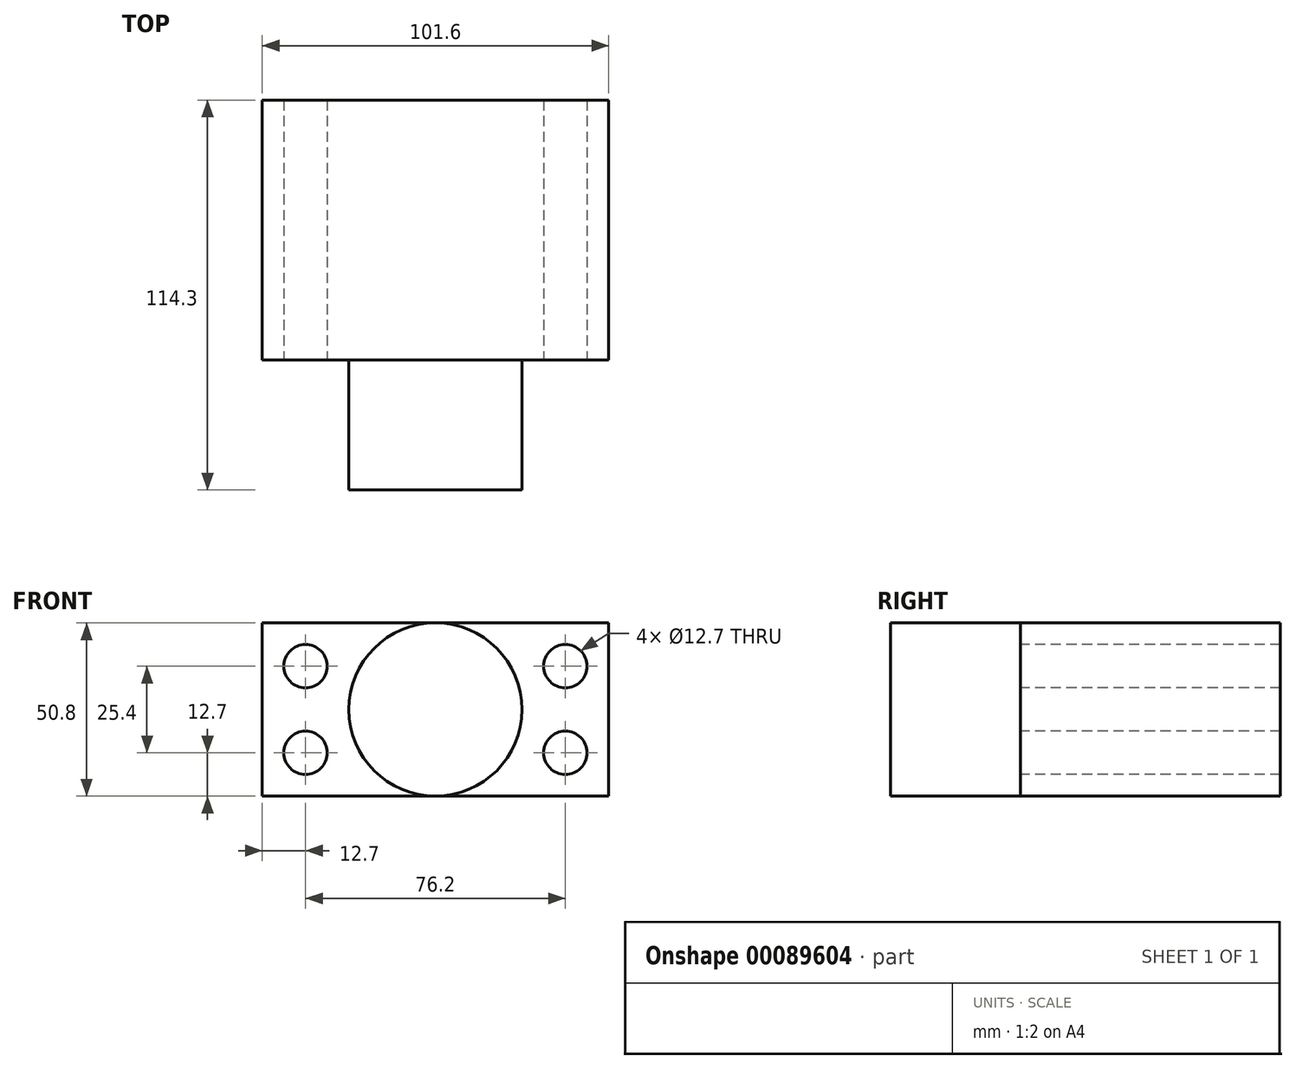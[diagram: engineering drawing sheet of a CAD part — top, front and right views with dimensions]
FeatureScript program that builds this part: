
annotation { "Feature Type Name" : "Feature", "Feature Type Description" : "" }
export const myFeature = defineFeature(function(context is Context, id is Id, definition is map)
    precondition{}
    {
        {
            var Q0;
            Q0=qCreatedBy(makeId("Front.planeOp"),FACE);
            var sketch = newSketch(context, id + "F0", { "sketchPlane" : qUnion([Q0])});
            skLineSegment(sketch, "E0", {"start": v(-50.8, 25.4) * mm, "end": v(50.8, 25.4) * mm});
            skLineSegment(sketch, "E1", {"start": v(50.8, 25.4) * mm, "end": v(50.8, -25.4) * mm});
            skLineSegment(sketch, "E2", {"start": v(50.8, -25.4) * mm, "end": v(-50.8, -25.4) * mm});
            skLineSegment(sketch, "E3", {"start": v(-50.8, 25.4) * mm, "end": v(-50.8, -25.4) * mm});
            skSolve(sketch);
        }
        {
            var Q0;
            Q0=makeQuery(id+"F0.imprint","IMPRINT",FACE,{"disambiguationData":[TD([[makeQuery(id+"F0.imprint","IMPRINT",EDGE,{"derivedFrom":sQuery(id+"F0.wireOp",EDGE,"E0")}),-1.0]])]});
            extrude(context, id + "F1", {"entities" : qUnion([Q0]), "depth" : 76.2 * mm});
        }
        {
            var Q0;
            Q0=makeQuery(id+"F1.opExtrude","CAP_FACE",FACE,{"disambiguationData":[OSD([sQuery(id+"F0.wireOp",EDGE,"E0"),sQuery(id+"F0.wireOp",EDGE,"E1"),sQuery(id+"F0.wireOp",EDGE,"E2"),sQuery(id+"F0.wireOp",EDGE,"E3")])],"isStart":false});
            var sketch = newSketch(context, id + "F2", { "sketchPlane" : qUnion([Q0])});
            skCircle(sketch, "E4", {"center": v(-38.1, 12.7) * mm, "radius": 6.35 * mm});
            skCircle(sketch, "E5", {"center": v(-38.1, -12.7) * mm, "radius": 6.35 * mm});
            skLineSegment(sketch, "E6", {"start": v(0, 0) * mm, "end": v(0, -43.53) * mm, "construction": true});
            skPoint(sketch, "E6.endSnap0", {"position": v(0, -25.4) * mm});
            skLineSegment(sketch, "E7", {"start": v(0, 0) * mm, "end": v(0, 43.06) * mm, "construction": true});
            skPoint(sketch, "E7.endSnap0", {"position": v(0, 25.4) * mm});
            skCircle(sketch, "E8.MirrorC", {"center": v(38.1, 12.7) * mm, "radius": 6.35 * mm});
            skCircle(sketch, "E9.MirrorC", {"center": v(38.1, -12.7) * mm, "radius": 6.35 * mm});
            skSolve(sketch);
        }
        {
            var Q0;
            Q0 = qSketchRegion(id + "F2", true);
            extrude(context, id + "F3", {"entities" : qUnion([Q0]), "operationType" : NewBodyOperationType.REMOVE, "endBound" : BoundingType.THROUGH_ALL, "oppositeDirection" : true, "depth" : 25.4 * mm});
        }
        {
            var Q0;
            Q0=qCreatedBy(makeId("Top.planeOp"),FACE);
            var sketch = newSketch(context, id + "F4", { "sketchPlane" : qUnion([Q0])});
            skLineSegment(sketch, "E10", {"start": v(0, -76.2) * mm, "end": v(0, -114.3) * mm});
            skLineSegment(sketch, "E11", {"start": v(0, -114.3) * mm, "end": v(-25.4, -114.3) * mm});
            skLineSegment(sketch, "E12", {"start": v(-25.4, -114.3) * mm, "end": v(-25.4, -76.2) * mm});
            skLineSegment(sketch, "E13", {"start": v(-25.4, -76.2) * mm, "end": v(0, -76.2) * mm});
            skSolve(sketch);
        }
        {
            var Q0;
            Q0=makeQuery(id+"F4.imprint","IMPRINT",FACE,{"disambiguationData":[TD([[makeQuery(id+"F4.imprint","IMPRINT",EDGE,{"derivedFrom":sQuery(id+"F4.wireOp",EDGE,"E10")}),-1.0]])]});
            var Q1;
            Q1=sQuery(id+"F4.wireOp",EDGE,"E10");
            revolve(context, id + "F5", {"operationType" : NewBodyOperationType.ADD, "entities" : qUnion([Q0]), "axis" : qUnion([Q1]), "revolveType" : RevolveType.FULL});
        }
    });
